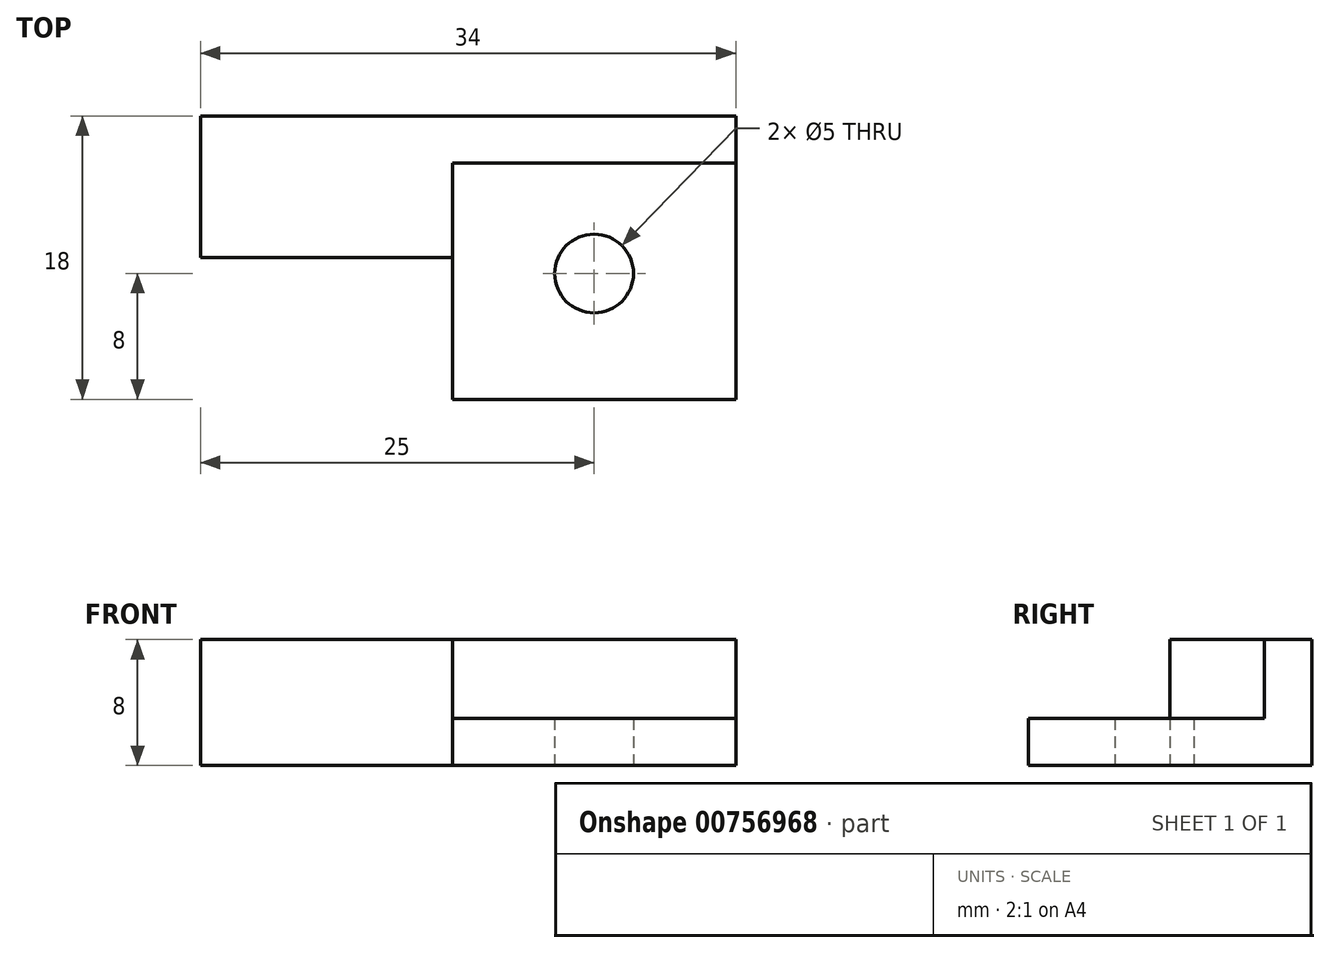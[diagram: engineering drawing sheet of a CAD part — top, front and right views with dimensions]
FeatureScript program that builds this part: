
annotation { "Feature Type Name" : "Feature", "Feature Type Description" : "" }
export const myFeature = defineFeature(function(context is Context, id is Id, definition is map)
    precondition{}
    {
        {
            var Q0;
            Q0=qCreatedBy(makeId("Top.planeOp"),FACE);
            var sketch = newSketch(context, id + "F0", { "sketchPlane" : qUnion([Q0])});
            skLineSegment(sketch, "E0", {"start": v(0, -18) * mm, "end": v(0, 0) * mm});
            skLineSegment(sketch, "E1", {"start": v(0, 0) * mm, "end": v(-34, 0) * mm});
            skLineSegment(sketch, "E2", {"start": v(0, -18) * mm, "end": v(-18, -18) * mm});
            skLineSegment(sketch, "E3", {"start": v(-18, -9) * mm, "end": v(-18, -18) * mm});
            skLineSegment(sketch, "E4", {"start": v(-18, -9) * mm, "end": v(-34, -9) * mm});
            skLineSegment(sketch, "E5", {"start": v(-34, 0) * mm, "end": v(-34, -9) * mm});
            skLineSegment(sketch, "E6", {"start": v(-18, -18) * mm, "end": v(0, 0) * mm, "construction": true});
            skLineSegment(sketch, "E7", {"start": v(-9, -9) * mm, "end": v(-9, 0) * mm, "construction": true});
            skCircle(sketch, "E8", {"center": v(-9, -10) * mm, "radius": 2.5 * mm});
            skSolve(sketch);
        }
        {
            var Q0;
            Q0 = qSketchRegion(id + "F0", true);
            extrude(context, id + "F1", {"entities" : qUnion([Q0]), "depth" : 8 * mm, "offsetDistance" : 25 * mm});
        }
        {
            var Q0;
            Q0=makeQuery(id+"F1.opExtrude","CAP_FACE",FACE,{"disambiguationData":[OSD([sQuery(id+"F0.wireOp",EDGE,"E0"),sQuery(id+"F0.wireOp",EDGE,"E1"),sQuery(id+"F0.wireOp",EDGE,"E2"),sQuery(id+"F0.wireOp",EDGE,"E3"),sQuery(id+"F0.wireOp",EDGE,"E4"),sQuery(id+"F0.wireOp",EDGE,"E5"),sQuery(id+"F0.wireOp",EDGE,"E8")])],"isStart":false});
            var sketch = newSketch(context, id + "F2", { "sketchPlane" : qUnion([Q0])});
            skLineSegment(sketch, "E9.0", {"start": v(-18, -9) * mm, "end": v(-18, -18) * mm});
            skLineSegment(sketch, "E9.1", {"start": v(0, -18) * mm, "end": v(-18, -18) * mm});
            skLineSegment(sketch, "E9.2", {"start": v(0, -18) * mm, "end": v(0, 0) * mm, "construction": true});
            skLineSegment(sketch, "E10", {"start": v(0, -18) * mm, "end": v(0, -3) * mm});
            skLineSegment(sketch, "E11", {"start": v(0, -3) * mm, "end": v(-18, -3) * mm});
            skLineSegment(sketch, "E12", {"start": v(-18, -3) * mm, "end": v(-18, -9) * mm});
            skSolve(sketch);
        }
        {
            var Q0;
            Q0 = qSketchRegion(id + "F2", true);
            extrude(context, id + "F3", {"entities" : qUnion([Q0]), "operationType" : NewBodyOperationType.REMOVE, "oppositeDirection" : true, "depth" : 5 * mm, "offsetDistance" : 25 * mm});
        }
    });
